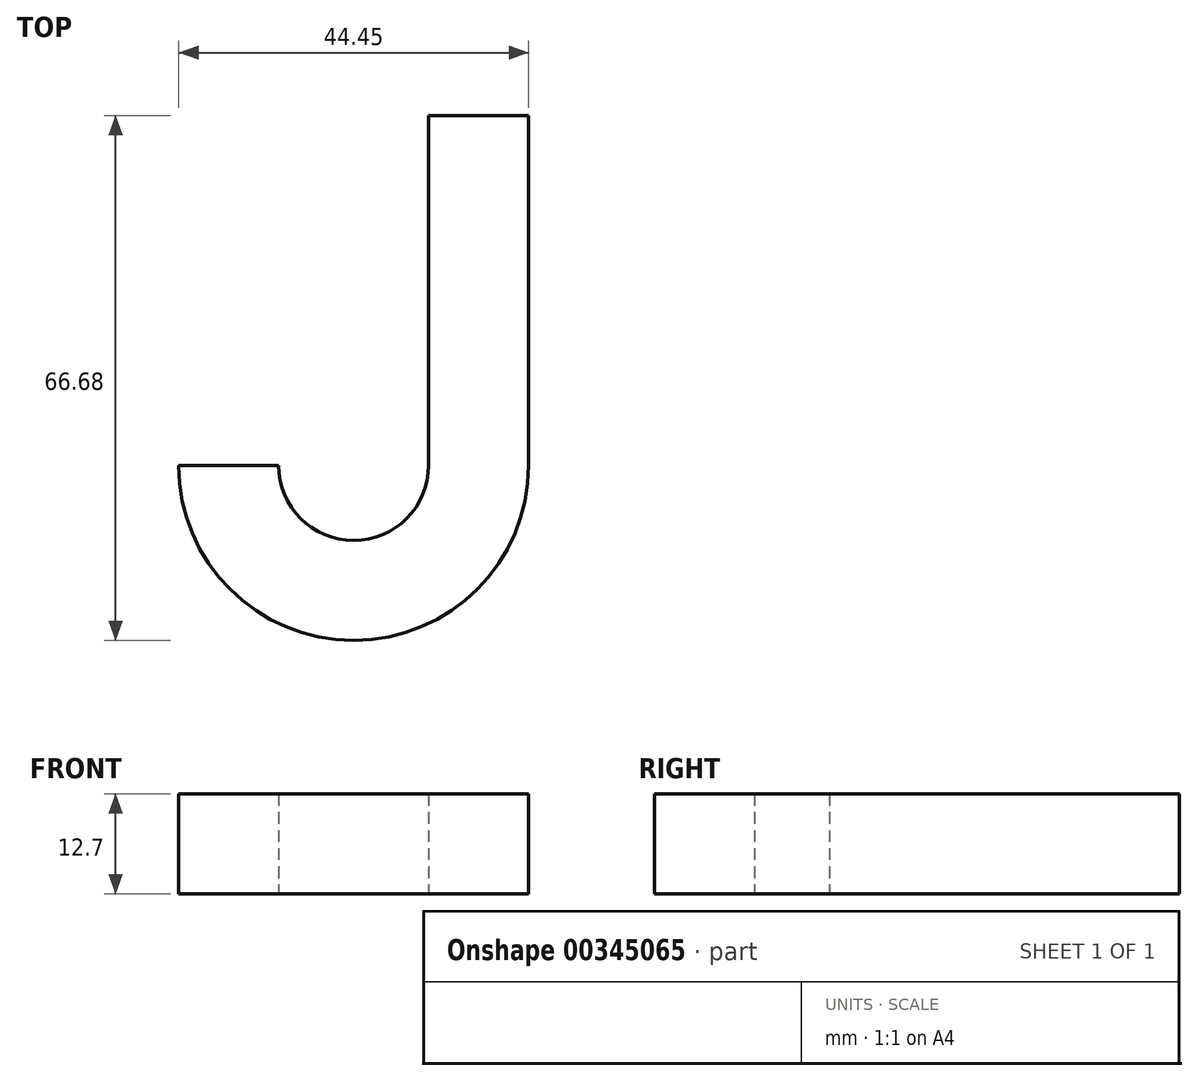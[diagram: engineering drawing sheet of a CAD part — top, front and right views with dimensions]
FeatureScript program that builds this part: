
annotation { "Feature Type Name" : "Feature", "Feature Type Description" : "" }
export const myFeature = defineFeature(function(context is Context, id is Id, definition is map)
    precondition{}
    {
        {
            var Q0;
            Q0=qCreatedBy(makeId("Top.planeOp"),FACE);
            var sketch = newSketch(context, id + "F0", { "sketchPlane" : qUnion([Q0])});
            skLineSegment(sketch, "E0.bottom", {"start": v(-6.35, 22.23) * mm, "end": v(6.35, 22.23) * mm});
            skLineSegment(sketch, "E0.top", {"start": v(-6.35, -22.23) * mm, "end": v(6.35, -22.23) * mm});
            skLineSegment(sketch, "E0.left", {"start": v(-6.35, 22.23) * mm, "end": v(-6.35, -22.23) * mm});
            skLineSegment(sketch, "E0.right", {"start": v(6.35, 22.23) * mm, "end": v(6.35, -22.23) * mm});
            skPoint(sketch, "E0.middle", {"position": v(0, 0) * mm});
            skArc(sketch, "E1", {"start": v(-25.4, -22.23) * mm, "mid": v(-15.87, -31.75) * mm, "end": v(-6.35, -22.23) * mm});
            skArc(sketch, "E2.0", {"start": v(-38.1, -22.23) * mm, "mid": v(-15.87, -44.45) * mm, "end": v(6.35, -22.23) * mm});
            skLineSegment(sketch, "E3", {"start": v(-38.1, -22.23) * mm, "end": v(-25.4, -22.23) * mm});
            skSolve(sketch);
        }
        {
            var Q0;
            Q0 = qSketchRegion(id + "F0", true);
            extrude(context, id + "F1", {"entities" : qUnion([Q0]), "depth" : 12.7 * mm});
        }
    });
